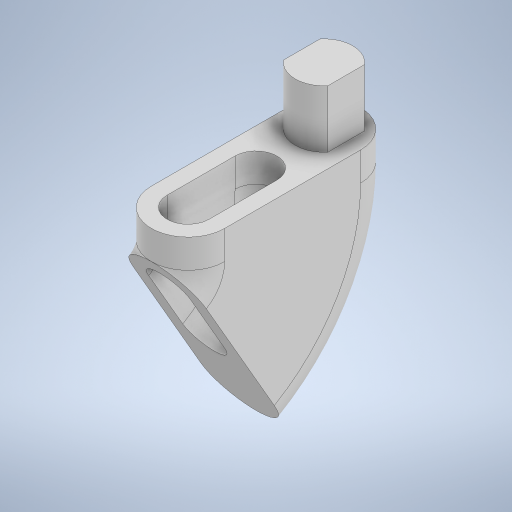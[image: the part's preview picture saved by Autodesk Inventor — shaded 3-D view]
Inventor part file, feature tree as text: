
AUTODESK INVENTOR PART (.ipt)
format: ipt  version: 2023 (Build 270158000, 158)  size: 297,472 bytes
history: native  units: mm
features: sketch x2, extrude x2, revolve x1
ambient origin geometry x8: Origin, YZ Plane, XZ Plane, XY Plane, X Axis, Y Axis, Z Axis, Center Point
bodies: Solido1 (feature_tree)
feature tree (5):
  sketch  "Schizzo1"
  extrude  "Estrusione1"  Depth=22.0mm
  extrude  "Estrusione2"  Depth=8.5mm
  revolve  "Rivoluzione1"
  sketch  "Schizzo4"
